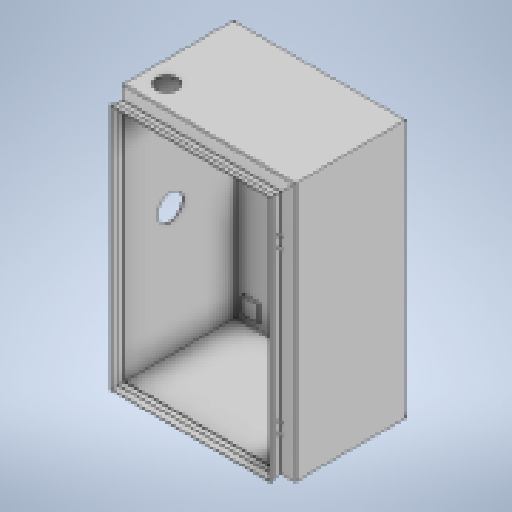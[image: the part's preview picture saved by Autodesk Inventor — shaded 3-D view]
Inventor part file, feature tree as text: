
AUTODESK INVENTOR PART (.ipt)
format: ipt  version: 2025.2 (Build 292293000, 293)  size: 934,912 bytes
history: native  units: mm
features: other x56, sketch x46, extrude x22, revolve x20, hole x4
ambient origin geometry x8: Origin, YZ Plane, XZ Plane, XY Plane, X Axis, Y Axis, Z Axis, Center Point
bodies: Solid1 (feature_tree)
feature tree (148):
  extrude  "Extrusion1"  Depth=300.0mm TaperAngle=0.0deg
  extrude  "Extrusion2"  Depth=300.0mm TaperAngle=0.0deg
  extrude  "Extrusion3"  Depth=3.25mm TaperAngle=0.0deg
  extrude  "Extrusion4"  Depth=3.25mm TaperAngle=0.0deg
  extrude  "Extrusion5"  Depth=15.297mm TaperAngle=0.0deg
  extrude  "Extrusion6"  Depth=15.297mm TaperAngle=0.0deg
  extrude  "Extrusion7"  Depth=15.297mm TaperAngle=0.0deg
  extrude  "Extrusion8"  Depth=15.297mm TaperAngle=0.0deg
  extrude  "Extrusion9"  TaperAngle=90.0deg  [1 undecoded]
  extrude  "Extrusion10"  TaperAngle=90.0deg  [1 undecoded]
  extrude  "Extrusion11"  TaperAngle=90.0deg  [1 undecoded]
  extrude  "Extrusion12"  TaperAngle=90.0deg  [1 undecoded]
  extrude  "Extrusion13"  TaperAngle=90.0deg  [1 undecoded]
  extrude  "Extrusion14"  TaperAngle=90.0deg  [1 undecoded]
  extrude  "Extrusion15"  TaperAngle=90.0deg  [1 undecoded]
  extrude  "Extrusion16"  TaperAngle=90.0deg  [1 undecoded]
  revolve  "Revolution1"  Angle=360.0deg
  revolve  "Revolution2"  Angle=360.0deg
  revolve  "Revolution3"  [1 undecoded]
  revolve  "Revolution4"  [1 undecoded]
  revolve  "Revolution5"  [1 undecoded]
  revolve  "Revolution6"  [1 undecoded]
  revolve  "Revolution7"  [1 undecoded]
  revolve  "Revolution8"  [1 undecoded]
  revolve  "Revolution9"  [1 undecoded]
  revolve  "Revolution10"  [1 undecoded]
  revolve  "Revolution11"  [1 undecoded]
  revolve  "Revolution12"  [1 undecoded]
  revolve  "Revolution13"  [1 undecoded]
  revolve  "Revolution14"  [1 undecoded]
  revolve  "Revolution15"  [1 undecoded]
  revolve  "Revolution16"  [1 undecoded]
  hole  "Hole1"  [1 undecoded]
  hole  "Hole2"  [1 undecoded]
  hole  "Hole3"  [1 undecoded]
  hole  "Hole4"  [1 undecoded]
  revolve  "Revolution17"  [1 undecoded]
  revolve  "Revolution18"  [1 undecoded]
  revolve  "Revolution19"  [1 undecoded]
  revolve  "Revolution20"  [1 undecoded]
  extrude  "Extrusion17"  [1 undecoded]
  extrude  "Extrusion18"  [1 undecoded]
  extrude  "Extrusion19"  [1 undecoded]
  extrude  "Extrusion20"  [1 undecoded]
  other  "GEHAEUSE_XY"
  other  "GEHAEUSE_YZ"
  other  "GEHAEUSE_ZX"
  other  "GEHAEUSE_X"
  other  "GEHAEUSE_Y"
  other  "GEHAEUSE_Z"
  other  "GEHAEUSE_Center"
  other  "to_HINGE_1_XY"
  other  "to_HINGE_1_YZ"
  other  "to_HINGE_1_ZX"
  other  "to_HINGE_1_X"
  other  "to_HINGE_1_Y"
  other  "to_HINGE_1_Z"
  other  "to_HINGE_1_Center"
  other  "to_HINGE_2_XY"
  other  "to_HINGE_2_YZ"
  other  "to_HINGE_2_ZX"
  other  "to_HINGE_2_X"
  other  "to_HINGE_2_Y"
  other  "to_HINGE_2_Z"
  other  "to_HINGE_2_Center"
  other  "to_L_Winkel_XY"
  other  "to_L_Winkel_YZ"
  other  "to_L_Winkel_ZX"
  other  "to_L_Winkel_X"
  other  "to_L_Winkel_Y"
  other  "to_L_Winkel_Z"
  other  "to_L_Winkel_Center"
  other  "to_L_Winkel_Bottom_XY"
  other  "to_L_Winkel_Bottom_YZ"
  other  "to_L_Winkel_Bottom_ZX"
  other  "to_L_Winkel_Bottom_X"
  other  "to_L_Winkel_Bottom_Y"
  other  "to_L_Winkel_Bottom_Z"
  other  "to_L_Winkel_Bottom_Center"
  other  "to_L_Winkel_Top_XY"
  other  "to_L_Winkel_Top_YZ"
  other  "to_L_Winkel_Top_ZX"
  other  "to_L_Winkel_Top_X"
  other  "to_L_Winkel_Top_Y"
  other  "to_L_Winkel_Top_Z"
  other  "to_L_Winkel_Top_Center"
  other  "to_L_Winkel_1_XY"
  other  "to_L_Winkel_1_YZ"
  other  "to_L_Winkel_1_ZX"
  other  "to_L_Winkel_1_X"
  other  "to_L_Winkel_1_Y"
  other  "to_L_Winkel_1_Z"
  other  "to_L_Winkel_1_Center"
  other  "to_MP_XY"
  other  "to_MP_YZ"
  other  "to_MP_ZX"
  other  "to_MP_X"
  other  "to_MP_Y"
  other  "to_MP_Z"
  other  "to_MP_Center"
  extrude  "Extrusion21"  [1 undecoded]
  extrude  "Extrusion22"  [1 undecoded]
  sketch  "Skizze_2"  dims[d4=200.0mm d5=0.0mm d6=300.0mm d7=0.0mm]
  sketch  "Sketch_1"  dims[d0=200.0mm d1=0.0mm d2=300.0mm d3=0.0mm]
  sketch  "Sketch_37"  dims[d44=90.0deg d45=90.0deg]
  sketch  "Sketch_38"  dims[d46=90.0deg d47=90.0deg]
  sketch  "Sketch_2"  dims[d8=3.25mm d9=0.0mm d10=3.25mm d11=0.0mm]
  sketch  "Sketch_9"  dims[d12=3.25mm d13=0.0mm d14=3.25mm d15=0.0mm]
  sketch  "Sketch_10"  dims[d16=15.297mm d17=0.0mm d18=15.297mm d19=0.0mm]
  sketch  "Sketch_11"  dims[d20=15.297mm d21=0.0mm d22=15.297mm d23=0.0mm]
  sketch  "Sketch_30"  dims[d24=15.297mm d25=0.0mm d26=15.297mm d27=0.0mm]
  sketch  "Sketch_31"  dims[d28=15.297mm d29=0.0mm d30=15.297mm d31=0.0mm]
  sketch  "Sketch_32"  dims[d32=90.0deg d33=90.0deg]
  sketch  "Sketch_33"  dims[d34=90.0deg d35=90.0deg]
  sketch  "Sketch_43"  dims[d48=3.2mm d49=6.0mm d50=4.0mm d51=2.0mm d52=90.0deg d53=1.25mm d54=0.0mm]
  sketch  "Sketch_44"  dims[d55=3.2mm d56=6.0mm d57=4.0mm d58=2.0mm d59=90.0deg d60=1.25mm d61=0.0mm]
  sketch  "Sketch_45"  dims[d62=3.2mm d63=6.0mm d64=4.0mm d65=2.0mm d66=90.0deg d67=1.25mm d68=0.0mm]
  sketch  "Sketch_46"  dims[d77=360.0deg d78=360.0deg]
  sketch  "Sketch_47"  dims[d82=1.2mm d83=0.0mm d84=1.2mm d85=0.0mm]
  sketch  "Sketch_48"  dims[d86=1.2mm d87=0.0mm d88=0.0mm]
  sketch  "Sketch_49"  dims[d89=0.0mm d90=0.0mm]
  sketch  "Sketch_50"  dims[d91=0.0mm d92=25.0mm]
  sketch  "Sketch_51"  dims[d93=75.0mm d94=25.0mm]
  sketch  "Sketch_52"  dims[d95=10.0mm d96=0.0mm d98=40.0mm]
  sketch  "Sketch_53"  dims[d99=10.0mm d100=0.0mm]
  sketch  "Sketch_54"
  sketch  "Sketch_55"
  sketch  "Sketch_56"
  sketch  "Sketch_57"
  sketch  "Sketch_58"
  sketch  "Sketch_59"
  sketch  "Sketch_60"
  sketch  "Sketch_61"
  sketch  "Sketch_62"
  sketch  "Sketch33"  dims[d36=90.0deg d37=90.0deg]
  sketch  "Sketch34"  dims[d38=90.0deg d39=90.0deg]
  sketch  "Sketch35"  dims[d40=90.0deg d41=90.0deg]
  sketch  "Sketch36"  dims[d42=90.0deg d43=90.0deg]
  sketch  "Sketch_75"
  sketch  "Sketch_76"
  sketch  "Sketch_77"
  sketch  "Sketch_78"
  sketch  "Sketch_79"
  sketch  "Sketch_80"
  sketch  "Sketch_81"
  sketch  "Sketch_82"
  sketch  "Sketch45"  dims[d69=3.2mm d70=6.0mm d71=4.0mm d72=2.0mm d73=90.0deg d74=1.25mm d75=0.0mm d76=360.0deg]
  sketch  "Sketch46"  dims[d79=360.0deg d80=1.2mm d81=0.0mm]
note: 36 required parameter values undecoded (feature->parameter linkage not recoverable at this tier; creation-order binding heuristic only, values carry confidence <= 0.55)